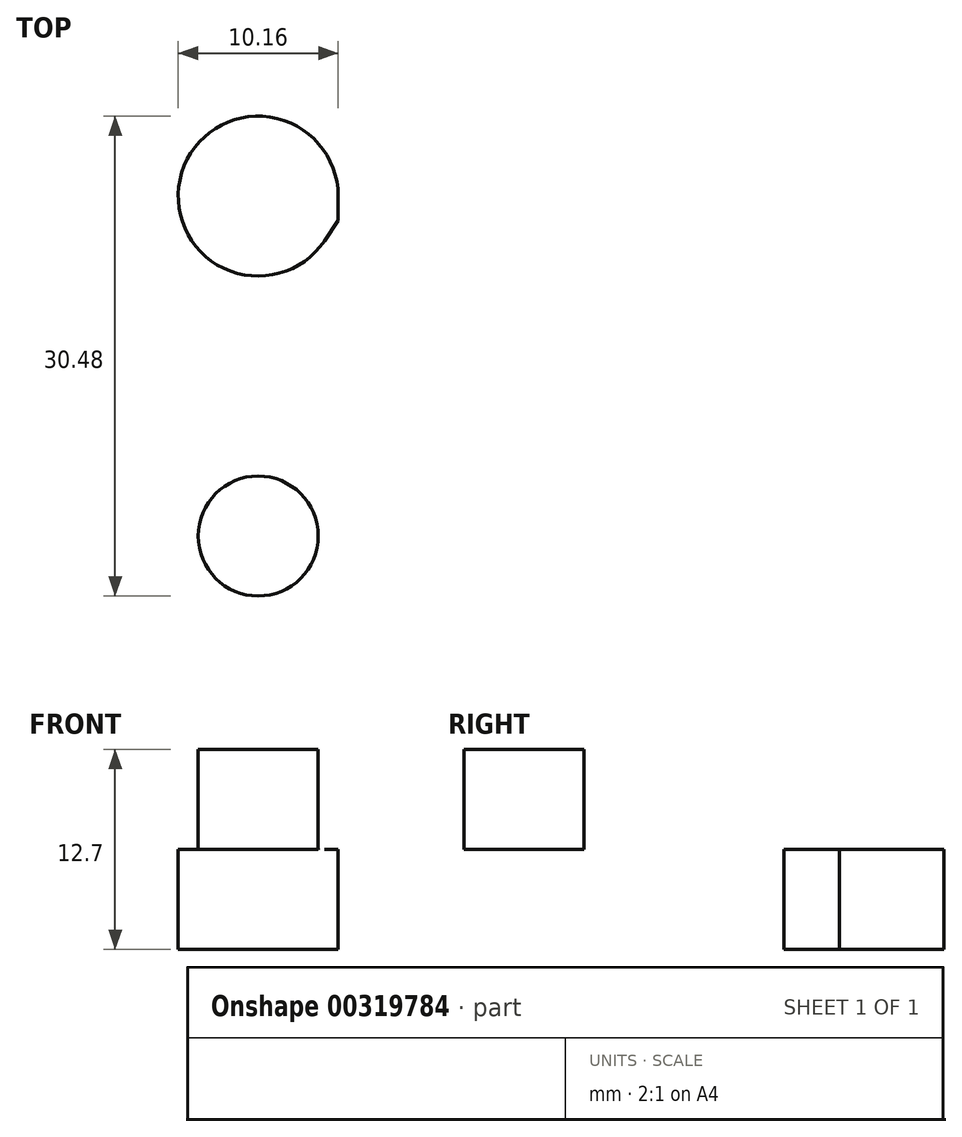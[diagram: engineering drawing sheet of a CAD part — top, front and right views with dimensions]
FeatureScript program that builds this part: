
annotation { "Feature Type Name" : "Feature", "Feature Type Description" : "" }
export const myFeature = defineFeature(function(context is Context, id is Id, definition is map)
    precondition{}
    {
        {
            var Q0;
            Q0=qCreatedBy(makeId("Top.planeOp"),FACE);
            var sketch = newSketch(context, id + "F0", { "sketchPlane" : qUnion([Q0])});
            skLineSegment(sketch, "E0", {"start": v(0, -30.93) * mm, "end": v(0, 3.36) * mm});
            skLineSegment(sketch, "E1", {"start": v(0, 3.36) * mm, "end": v(22.73, 37.05) * mm});
            skPoint(sketch, "E2", {"position": v(0, -18.23) * mm});
            skArc(sketch, "E3.0.startCap", {"start": v(4.21, 0.52) * mm, "mid": v(-2.84, -0.85) * mm, "end": v(-4.21, 6.2) * mm});
            skArc(sketch, "E3.0.endCap", {"start": v(18.51, 39.89) * mm, "mid": v(25.57, 41.26) * mm, "end": v(26.94, 34.2) * mm});
            skLineSegment(sketch, "E3.0.left", {"start": v(-4.21, 6.2) * mm, "end": v(18.51, 39.89) * mm});
            skLineSegment(sketch, "E3.0.right", {"start": v(4.21, 0.52) * mm, "end": v(26.94, 34.2) * mm});
            skArc(sketch, "E3.1.startCap", {"start": v(5.08, -30.93) * mm, "mid": v(0, -36.01) * mm, "end": v(-5.08, -30.93) * mm});
            skArc(sketch, "E3.1.endCap", {"start": v(-5.08, 3.36) * mm, "mid": v(0, 8.44) * mm, "end": v(5.08, 3.36) * mm});
            skLineSegment(sketch, "E3.1.left", {"start": v(-5.08, -30.93) * mm, "end": v(-5.08, 3.36) * mm});
            skLineSegment(sketch, "E3.1.right", {"start": v(5.08, -30.93) * mm, "end": v(5.08, 3.36) * mm});
            skSolve(sketch);
        }
        {
            var Q0;
            {var subQ1=sQuery(id+"F0.wireOp",EDGE,"E3.0.endCap");Q0=makeQuery(id+"F0.imprint","IMPRINT",FACE,{"disambiguationData":[TD([[makeQuery(id+"F0.imprint","IMPRINT",EDGE,{"derivedFrom":subQ1}),-1.0]])]});}
            var Q1;
            {var subQ3=sQuery(id+"F0.wireOp",EDGE,"E0");var subQ7=sQuery(id+"F0.wireOp",EDGE,"E1");var subQ8=makeQuery(id+"F0.imprint","INTERSECT",VERTEX,{"derivedFrom":[subQ3,subQ7]});Q1=makeQuery(id+"F0.imprint","IMPRINT",FACE,{"disambiguationData":[TD([[makeQuery(id+"F0.imprint","IMPRINT",EDGE,{"disambiguationData":[TD([[subQ8,1.0]])],"derivedFrom":subQ3}),-1.0]])]});}
            var Q2;
            {var subQ5=sQuery(id+"F0.wireOp",EDGE,"E3.1.startCap");Q2=makeQuery(id+"F0.imprint","IMPRINT",FACE,{"disambiguationData":[TD([[makeQuery(id+"F0.imprint","IMPRINT",EDGE,{"derivedFrom":subQ5}),-1.0]])]});}
            var Q3;
            {var subQ4=sQuery(id+"F0.wireOp",EDGE,"E0");var subQ6=sQuery(id+"F0.wireOp",EDGE,"E1");var subQ7=makeQuery(id+"F0.imprint","INTERSECT",VERTEX,{"derivedFrom":[subQ4,subQ6]});Q3=makeQuery(id+"F0.imprint","IMPRINT",FACE,{"disambiguationData":[TD([[makeQuery(id+"F0.imprint","IMPRINT",EDGE,{"disambiguationData":[TD([[subQ7,1.0]])],"derivedFrom":subQ4}),1.0]])]});}
            var Q4;
            Q4 = qConstructionFilter(qBodyType(qCreatedBy(id + "F0" ,EDGE), BodyType.WIRE), ConstructionObject.NO);
            extrude(context, id + "F1", {"entities" : qUnion([Q0, Q1, Q2, Q3]), "surfaceEntities" : qUnion([Q4]), "depth" : 6.35 * mm});
        }
        {
            var Q0;
            Q0=makeQuery(id+"F1.opExtrude","CAP_FACE",FACE,{"disambiguationData":[OSD([sQuery(id+"F0.wireOp",EDGE,"E3.0.endCap"),sQuery(id+"F0.wireOp",EDGE,"E3.0.left"),sQuery(id+"F0.wireOp",EDGE,"E3.0.right"),sQuery(id+"F0.wireOp",EDGE,"E3.1.startCap"),sQuery(id+"F0.wireOp",EDGE,"E3.1.endCap"),sQuery(id+"F0.wireOp",EDGE,"E3.1.left"),sQuery(id+"F0.wireOp",EDGE,"E3.1.right")])],"isStart":false});
            var sketch = newSketch(context, id + "F2", { "sketchPlane" : qUnion([Q0])});
            skCircle(sketch, "E4", {"center": v(0, -18.23) * mm, "radius": 3.81 * mm});
            skSolve(sketch);
        }
        {
            var Q0;
            Q0=makeQuery(id+"F2.imprint","IMPRINT",FACE,{"disambiguationData":[TD([[makeQuery(id+"F2.imprint","IMPRINT",EDGE,{"derivedFrom":sQuery(id+"F2.wireOp",EDGE,"E4")}),1.0]])]});
            var Q1;
            Q1=sQuery(id+"F2.wireOp",EDGE,"E4");
            extrude(context, id + "F3", {"entities" : qUnion([Q0]), "operationType" : NewBodyOperationType.ADD, "surfaceEntities" : qUnion([Q1]), "depth" : 6.35 * mm});
        }
        {
            var Q0;
            Q0=sQuery(id+"F0.wireOp",VERTEX,"E2");
            var Q1;
            Q1=makeQuery(id+"F1.opExtrude","SWEPT_BODY",BODY,{"disambiguationData":[OSD([sQuery(id+"F0.wireOp",EDGE,"E3.0.endCap"),sQuery(id+"F0.wireOp",EDGE,"E3.0.left"),sQuery(id+"F0.wireOp",EDGE,"E3.0.right"),sQuery(id+"F0.wireOp",EDGE,"E3.1.startCap"),sQuery(id+"F0.wireOp",EDGE,"E3.1.endCap"),sQuery(id+"F0.wireOp",EDGE,"E3.1.left"),sQuery(id+"F0.wireOp",EDGE,"E3.1.right")])]});
            hole(context, id + "F4", {"style" : HoleStyle.C_SINK, "endStyle" : HoleEndStyle.THROUGH, "oppositeDirection" : true, "holeDiameter" : 2.03 * mm, "cSinkDiameter" : 3.17 * mm, "cSinkAngle" : 82 * degree, "tappedDepth" : 12.7 * mm, "tapClearance" : 3, "locations" : qUnion([Q0]), "scope" : qUnion([Q1])});
        }
        {
            var Q0;
            Q0=sQuery(id+"F0.wireOp",VERTEX,"E3.1.startCap.center");
            var Q1;
            Q1=makeQuery(id+"F1.opExtrude","SWEPT_BODY",BODY,{"disambiguationData":[OSD([sQuery(id+"F0.wireOp",EDGE,"E3.0.endCap"),sQuery(id+"F0.wireOp",EDGE,"E3.0.left"),sQuery(id+"F0.wireOp",EDGE,"E3.0.right"),sQuery(id+"F0.wireOp",EDGE,"E3.1.startCap"),sQuery(id+"F0.wireOp",EDGE,"E3.1.endCap"),sQuery(id+"F0.wireOp",EDGE,"E3.1.left"),sQuery(id+"F0.wireOp",EDGE,"E3.1.right")])]});
            hole(context, id + "F5", {"style" : HoleStyle.SIMPLE, "endStyle" : HoleEndStyle.THROUGH, "oppositeDirection" : true, "holeDiameter" : 2.03 * mm, "tappedDepth" : 12.7 * mm, "tapClearance" : 3, "locations" : qUnion([Q0]), "scope" : qUnion([Q1])});
        }
    });
